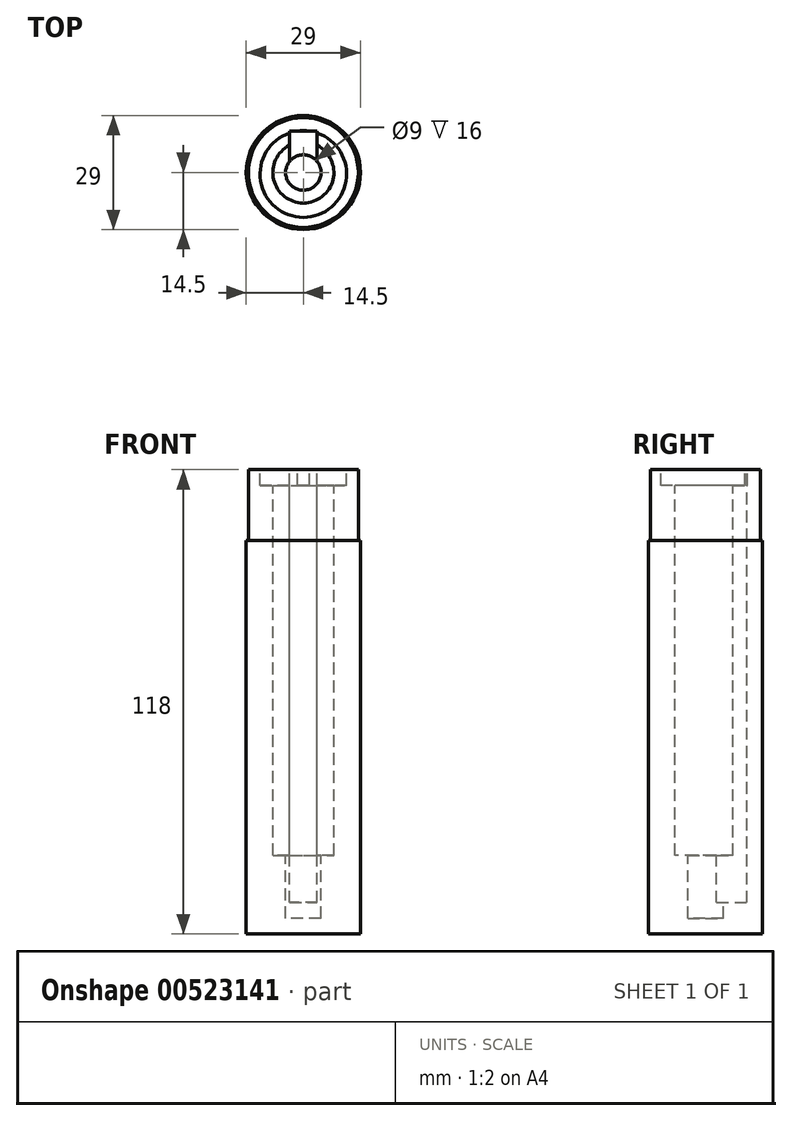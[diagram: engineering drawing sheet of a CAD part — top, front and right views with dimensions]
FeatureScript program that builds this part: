
annotation { "Feature Type Name" : "Feature", "Feature Type Description" : "" }
export const myFeature = defineFeature(function(context is Context, id is Id, definition is map)
    precondition{}
    {
        {
            var Q0;
            Q0=qCreatedBy(makeId("Top.planeOp"),FACE);
            var sketch = newSketch(context, id + "F0", { "sketchPlane" : qUnion([Q0])});
            skCircle(sketch, "E0", {"center": v(0, 0) * mm, "radius": 13.95 * mm});
            skSolve(sketch);
        }
        {
            var Q0;
            Q0=makeQuery(id+"F0.imprint","IMPRINT",FACE,{"disambiguationData":[TD([[makeQuery(id+"F0.imprint","IMPRINT",EDGE,{"derivedFrom":sQuery(id+"F0.wireOp",EDGE,"E0")}),1.0]])]});
            extrude(context, id + "F1", {"entities" : qUnion([Q0]), "depth" : 118 * mm, "offsetDistance" : 25 * mm});
        }
        {
            var Q0;
            Q0=makeQuery(id+"F1.opExtrude","CAP_FACE",FACE,{"disambiguationData":[OSD([sQuery(id+"F0.wireOp",EDGE,"E0")])],"isStart":false});
            var sketch = newSketch(context, id + "F2", { "sketchPlane" : qUnion([Q0])});
            skCircle(sketch, "E1", {"center": v(0, -0.4) * mm, "radius": 11 * mm});
            skSolve(sketch);
        }
        {
            var Q0;
            Q0=makeQuery(id+"F2.imprint","IMPRINT",FACE,{"disambiguationData":[TD([[makeQuery(id+"F2.imprint","IMPRINT",EDGE,{"derivedFrom":sQuery(id+"F2.wireOp",EDGE,"E1")}),1.0]])]});
            extrude(context, id + "F3", {"entities" : qUnion([Q0]), "operationType" : NewBodyOperationType.REMOVE, "oppositeDirection" : true, "depth" : 4 * mm});
        }
        {
            var Q0;
            Q0=makeQuery(id+"F3.boolean.opBoolean","COPY",FACE,{"derivedFrom":makeQuery(id+"F3.opExtrude","CAP_FACE",FACE,{"disambiguationData":[OSD([sQuery(id+"F2.wireOp",EDGE,"E1")])],"isStart":false})});
            var sketch = newSketch(context, id + "F4", { "sketchPlane" : qUnion([Q0])});
            skCircle(sketch, "E2", {"center": v(0, 0) * mm, "radius": 7.75 * mm});
            skSolve(sketch);
        }
        {
            var Q0;
            Q0=makeQuery(id+"F4.imprint","IMPRINT",FACE,{"disambiguationData":[TD([[makeQuery(id+"F4.imprint","IMPRINT",EDGE,{"derivedFrom":sQuery(id+"F4.wireOp",EDGE,"E2")}),1.0]])]});
            extrude(context, id + "F5", {"entities" : qUnion([Q0]), "operationType" : NewBodyOperationType.REMOVE, "oppositeDirection" : true, "depth" : 94 * mm, "offsetDistance" : 25 * mm});
        }
        {
            var Q0;
            Q0=makeQuery(id+"F1.opExtrude","CAP_FACE",FACE,{"disambiguationData":[OSD([sQuery(id+"F0.wireOp",EDGE,"E0")])],"isStart":false});
            var sketch = newSketch(context, id + "F6", { "sketchPlane" : qUnion([Q0])});
            skLineSegment(sketch, "E3", {"start": v(0, 0) * mm, "end": v(3.5, 0) * mm});
            skLineSegment(sketch, "E4", {"start": v(3.5, 0) * mm, "end": v(3.5, 10.5) * mm});
            skLineSegment(sketch, "E5", {"start": v(0, 0) * mm, "end": v(-3.5, 0) * mm});
            skLineSegment(sketch, "E6", {"start": v(-3.5, 0) * mm, "end": v(-3.5, 10.5) * mm});
            skLineSegment(sketch, "E7", {"start": v(-3.5, 10.5) * mm, "end": v(3.5, 10.5) * mm});
            skSolve(sketch);
        }
        {
            var Q0;
            Q0=qSketchRegion(id+"F6",true);
            extrude(context, id + "F7", {"entities" : qUnion([Q0]), "operationType" : NewBodyOperationType.REMOVE, "oppositeDirection" : true, "depth" : 115 * mm, "offsetDistance" : 25 * mm});
        }
        {
            var Q0;
            Q0=qCreatedBy(makeId("Top.planeOp"),FACE);
            var sketch = newSketch(context, id + "F8", { "sketchPlane" : qUnion([Q0])});
            skCircle(sketch, "E8", {"center": v(0, 0) * mm, "radius": 14.5 * mm});
            skSolve(sketch);
        }
        {
            var Q0;
            Q0=makeQuery(id+"F8.imprint","IMPRINT",FACE,{"disambiguationData":[TD([[makeQuery(id+"F8.imprint","IMPRINT",EDGE,{"derivedFrom":sQuery(id+"F8.wireOp",EDGE,"E8")}),1.0]])]});
            extrude(context, id + "F9", {"entities" : qUnion([Q0]), "operationType" : NewBodyOperationType.ADD, "depth" : 100 * mm, "offsetDistance" : 25 * mm});
        }
        {
            var Q0;
            Q0=qSketchRegion(id+"F4",true);
            extrude(context, id + "F10", {"entities" : qUnion([Q0]), "operationType" : NewBodyOperationType.REMOVE, "oppositeDirection" : true, "depth" : 94 * mm, "offsetDistance" : 25 * mm});
        }
        {
            var Q0;
            Q0=qSketchRegion(id+"F6",true);
            extrude(context, id + "F11", {"entities" : qUnion([Q0]), "operationType" : NewBodyOperationType.REMOVE, "oppositeDirection" : true, "depth" : 110 * mm, "offsetDistance" : 25 * mm});
        }
        {
            var Q0;
            Q0=makeQuery(id+"F10.boolean.opBoolean","COPY",FACE,{"derivedFrom":makeQuery(id+"F10.opExtrude","CAP_FACE",FACE,{"disambiguationData":[OSD([sQuery(id+"F4.wireOp",EDGE,"E2")])],"isStart":false})});
            var sketch = newSketch(context, id + "F12", { "sketchPlane" : qUnion([Q0])});
            skCircle(sketch, "E9", {"center": v(0, 0) * mm, "radius": 4.5 * mm});
            skSolve(sketch);
        }
        {
            var Q0;
            Q0 = qSketchRegion(id + "F12", true);
            extrude(context, id + "F13", {"entities" : qUnion([Q0]), "operationType" : NewBodyOperationType.REMOVE, "oppositeDirection" : true, "depth" : 16 * mm, "offsetDistance" : 25 * mm});
        }
    });
